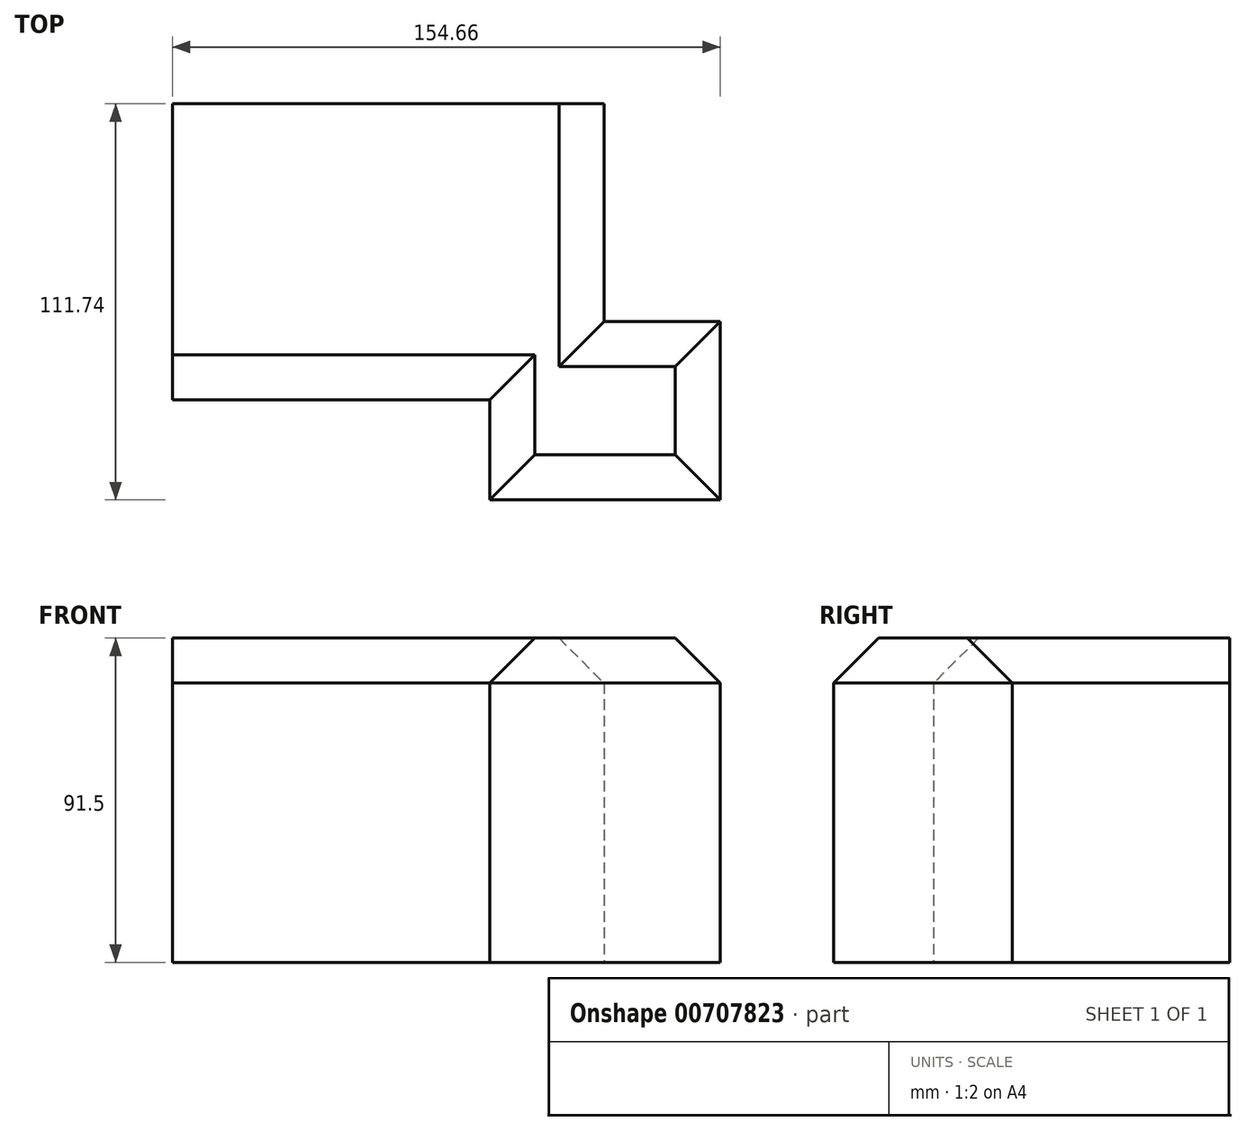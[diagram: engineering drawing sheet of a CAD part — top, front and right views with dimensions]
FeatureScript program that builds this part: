
annotation { "Feature Type Name" : "Feature", "Feature Type Description" : "" }
export const myFeature = defineFeature(function(context is Context, id is Id, definition is map)
    precondition{}
    {
        {
            var Q0;
            Q0=qCreatedBy(makeId("Top.planeOp"),FACE);
            var sketch = newSketch(context, id + "F0", { "sketchPlane" : qUnion([Q0])});
            skLineSegment(sketch, "E0.bottom", {"start": v(0, 50.33) * mm, "end": v(65.04, 50.33) * mm});
            skLineSegment(sketch, "E0.top", {"start": v(0, 0) * mm, "end": v(65.04, 0) * mm});
            skLineSegment(sketch, "E0.left", {"start": v(0, 50.33) * mm, "end": v(0, 0) * mm});
            skLineSegment(sketch, "E0.right", {"start": v(65.04, 50.33) * mm, "end": v(65.04, 0) * mm});
            skLineSegment(sketch, "E1.bottom", {"start": v(32.16, 28.17) * mm, "end": v(-89.62, 28.17) * mm});
            skLineSegment(sketch, "E1.top", {"start": v(32.16, 111.74) * mm, "end": v(-89.62, 111.74) * mm});
            skLineSegment(sketch, "E1.left", {"start": v(32.16, 28.17) * mm, "end": v(32.16, 111.74) * mm});
            skLineSegment(sketch, "E1.right", {"start": v(-89.62, 28.17) * mm, "end": v(-89.62, 111.74) * mm});
            skSolve(sketch);
        }
        {
            var Q0;
            Q0 = qSketchRegion(id + "F0", true);
            extrude(context, id + "F1", {"entities" : qUnion([Q0]), "depth" : 91.5 * mm, "offsetDistance" : 25.4 * mm});
        }
        {
            var Q0;
            Q0=makeQuery(id+"F1.opExtrude","CAP_EDGE",EDGE,{"disambiguationData":[OSD([sQuery(id+"F0.wireOp",EDGE,"E1.bottom")])],"isStart":false});
            var Q1;
            Q1=makeQuery(id+"F1.opExtrude","CAP_EDGE",EDGE,{"disambiguationData":[OSD([sQuery(id+"F0.wireOp",EDGE,"E0.left")])],"isStart":false});
            var Q2;
            Q2=makeQuery(id+"F1.opExtrude","CAP_EDGE",EDGE,{"disambiguationData":[OSD([sQuery(id+"F0.wireOp",EDGE,"E0.top")])],"isStart":false});
            var Q3;
            Q3=makeQuery(id+"F1.opExtrude","CAP_EDGE",EDGE,{"disambiguationData":[OSD([sQuery(id+"F0.wireOp",EDGE,"E0.right")])],"isStart":false});
            var Q4;
            Q4=makeQuery(id+"F1.opExtrude","CAP_EDGE",EDGE,{"disambiguationData":[OSD([sQuery(id+"F0.wireOp",EDGE,"E0.bottom")])],"isStart":false});
            var Q5;
            Q5=makeQuery(id+"F1.opExtrude","CAP_EDGE",EDGE,{"disambiguationData":[OSD([sQuery(id+"F0.wireOp",EDGE,"E1.left")])],"isStart":false});
            chamfer(context, id + "F2", {"entities" : qUnion([Q0, Q1, Q2, Q3, Q4, Q5]), "width" : 12.7 * mm, "tangentPropagation" : true});
        }
    });
